# Revit family: Legrand Export Universal Columns
name_source: partatom
category: Installations électriques
units: mm (PartAtom-declared; Revit-internal decimal feet)

## family parameters
Basée sur le plan de construction = Non
Conserver l'orientation des annotations = Non
Cote de connecteur circulaire = Utiliser le diamètre
Couper avec des vides une fois chargée = Non
Partagée = Non
Point de calcul de pièce = Non
Toujours verticalement = Oui
Type d'élément = Normal

## types (12) — shared parameters
Fabricant = LEGRAND
Largeur = 75 mm
Main Material = Aluminum
Standard = Universal
Séparateur = 35 mm  [stored 0.114829 ft]
zero-valued in all types: Elévation par défaut

## per-type parameters (varying)
| type | 1 CPT | 2 CPT | Description | Finishing | Finishing kit for telescopic pole | H1 | HC | Longueur | Matériau couvercle | Matériaux corps | Modèle | Number of compartments |
| Column 1cpt CV80 2,67m White | Oui | Non | universal Column 1 compartment 2,67m White | White | Finishing kit for telescopic pole : White CV perche for Column | 2700 mm | 2660 mm  [stored 8.72703 ft] | 82 mm | Legrand - Plastique blanc | Legrand - Aluminium blanc | LG-653110 | 1 compartment |
| Column 1cpt CV80 2,67m Alu | Oui | Non | universal Column 1 compartment 2,67m Aluminium | Aluminum | Finishing kit for telescopic pole : Grey CV  perche for Column | 2700 mm | 2660 mm  [stored 8.72703 ft] | 82 mm | Legrand - Plastique gris | Legrand - Aluminium gris | LG-653111 | 1 compartment |
| Column 1cpt CV80 2,67m Black | Oui | Non | universal Column 1 compartment 2,67m Black | Black | Finishing kit for telescopic pole : Black CV  perche for Column | 2700 mm | 2660 mm  [stored 8.72703 ft] | 82 mm | Legrand - Plastique noir | Legrand - Aluminium noir | LG-653112 | 1 compartment |
| Column 1cpt CV80 3,92m White | Oui | Non | universal Column 1 compartment 3,92m White | White | Finishing kit for telescopic pole : White CV perche for Column | 3900 mm  [stored 12.7953 ft] | 3860 mm  [stored 12.664 ft] | 82 mm | Legrand - Plastique blanc | Legrand - Aluminium blanc | LG-653113 | 1 compartment |
| Column 1cpt CV80 3,92m Alu | Oui | Non | universal Column 1 compartment 3,92m Aluminium | Aluminum | Finishing kit for telescopic pole : Grey CV  perche for Column | 3900 mm  [stored 12.7953 ft] | 3860 mm  [stored 12.664 ft] | 82 mm | Legrand - Plastique gris | Legrand - Aluminium gris | LG-653114 | 1 compartment |
| Column 1cpt CV80 3,92m Black | Oui | Non | universal Column 1 compartment 3,92m Black | Black | Finishing kit for telescopic pole : Black CV  perche for Column | 3900 mm  [stored 12.7953 ft] | 3860 mm  [stored 12.664 ft] | 82 mm | Legrand - Plastique noir | Legrand - Aluminium noir | LG-653115 | 1 compartment |
| Column 2 cpts CV80 2,67M White | Non | Oui | universal Column 2 compartments 2,67m White | White | Finishing kit for telescopic pole : White CV perche for Column | 2700 mm | 2660 mm  [stored 8.72703 ft] | 125 mm | Legrand - Plastique blanc | Legrand - Aluminium blanc | LG-653130 | 2 compartments |
| Column 2 cpts CV80 2,67M Alu | Non | Oui | universal Column 2 compartments 2,67m Aluminium | Aluminum | Finishing kit for telescopic pole : Grey CV  perche for Column | 2700 mm | 2660 mm  [stored 8.72703 ft] | 125 mm | Legrand - Plastique gris | Legrand - Aluminium gris | LG-653131 | 2 compartments |
| Column 2 cpts CV80 2,67M Black | Non | Oui | universal Column 2 compartments 2,67m Black | Black | Finishing kit for telescopic pole : Black CV  perche for Column | 2700 mm | 2660 mm  [stored 8.72703 ft] | 125 mm | Legrand - Plastique noir | Legrand - Aluminium noir | LG-653132 | 2 compartments |
| Column 2 cpts CV80 3,92M White | Non | Oui | universal Column 2 compartments 3,92m White | White | Finishing kit for telescopic pole : White CV perche for Column | 3900 mm  [stored 12.7953 ft] | 3860 mm  [stored 12.664 ft] | 125 mm | Legrand - Plastique blanc | Legrand - Aluminium blanc | LG-653133 | 2 compartments |
| Column 2 cpts CV80 3,92M Alu | Non | Oui | universal Column 2 compartments 3,92m Aluminium | Aluminum | Finishing kit for telescopic pole : Grey CV  perche for Column | 3900 mm  [stored 12.7953 ft] | 3860 mm  [stored 12.664 ft] | 125 mm | Legrand - Plastique gris | Legrand - Aluminium gris | LG-653134 | 2 compartments |
| Column 2 cpts CV80 3,92M Black | Non | Oui | universal Column 2 compartments 3,92m Black | Black | Finishing kit for telescopic pole : Black CV  perche for Column | 3900 mm  [stored 12.7953 ft] | 3860 mm  [stored 12.664 ft] | 125 mm | Legrand - Plastique noir | Legrand - Aluminium noir | LG-653135 | 2 compartments |

note: [stored X ft] marks values corroborated as IEEE doubles in the binary element streams (Revit-internal decimal feet)
